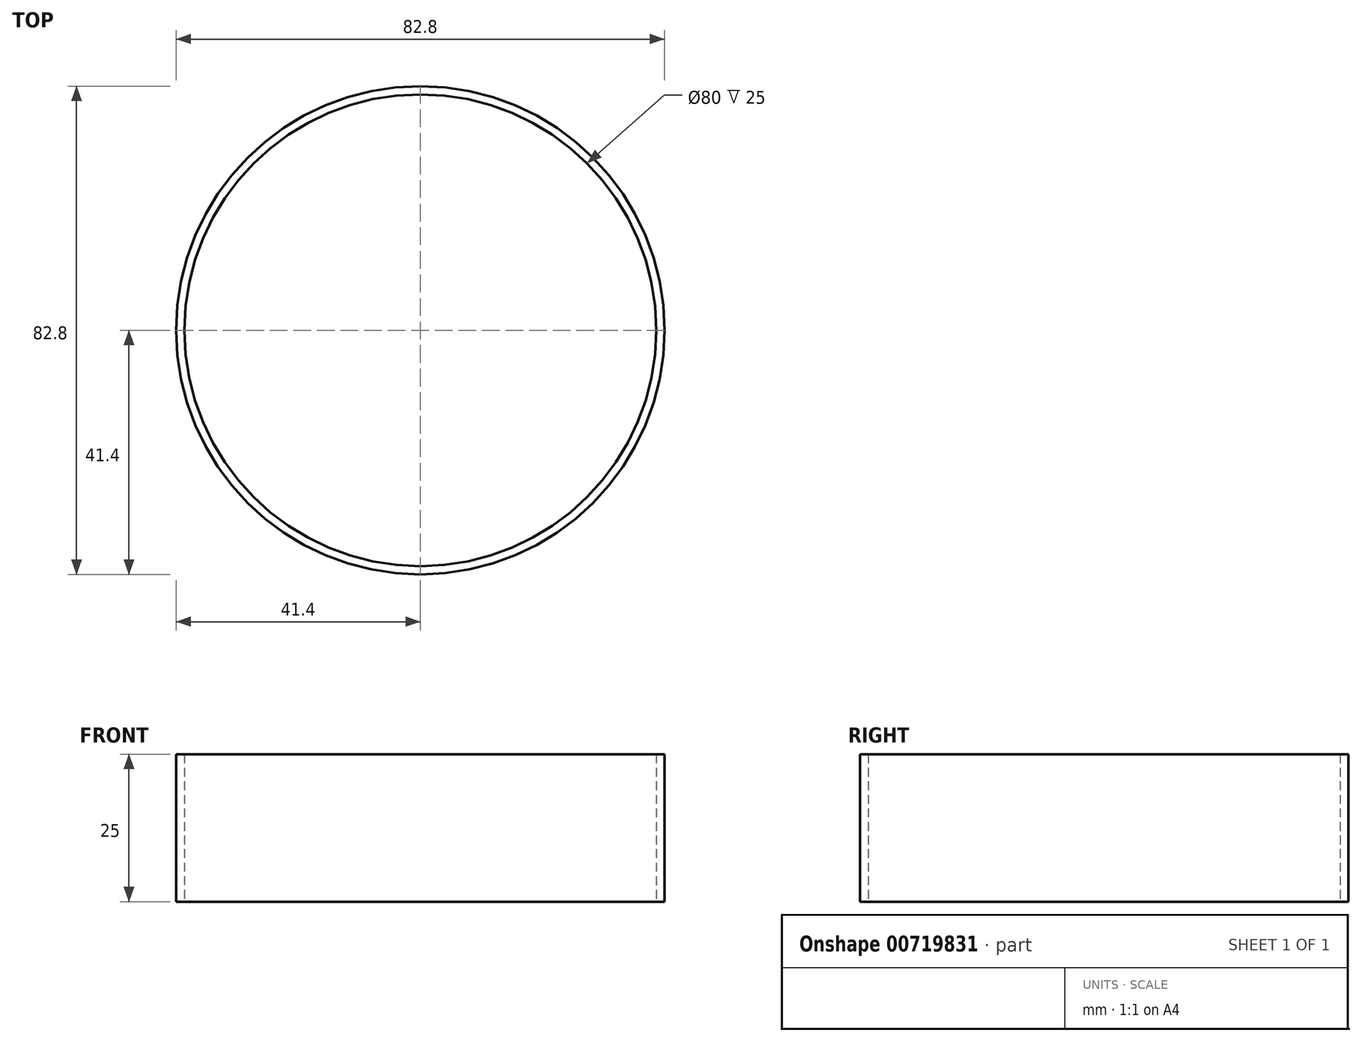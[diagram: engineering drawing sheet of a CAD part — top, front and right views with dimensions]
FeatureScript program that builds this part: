
annotation { "Feature Type Name" : "Feature", "Feature Type Description" : "" }
export const myFeature = defineFeature(function(context is Context, id is Id, definition is map)
    precondition{}
    {
        {
            var Q0;
            Q0=qCreatedBy(makeId("Top.planeOp"),FACE);
            var sketch = newSketch(context, id + "F0", { "sketchPlane" : qUnion([Q0])});
            skCircle(sketch, "E0", {"center": v(0, 0) * mm, "radius": 40 * mm});
            skCircle(sketch, "E1", {"center": v(0, 0) * mm, "radius": 41.4 * mm});
            skSolve(sketch);
        }
        {
            var Q0;
            Q0 = qSketchRegion(id + "F0", true);
            extrude(context, id + "F1", {"entities" : qUnion([Q0]), "depth" : 25 * mm, "offsetDistance" : 25 * mm});
        }
    });
